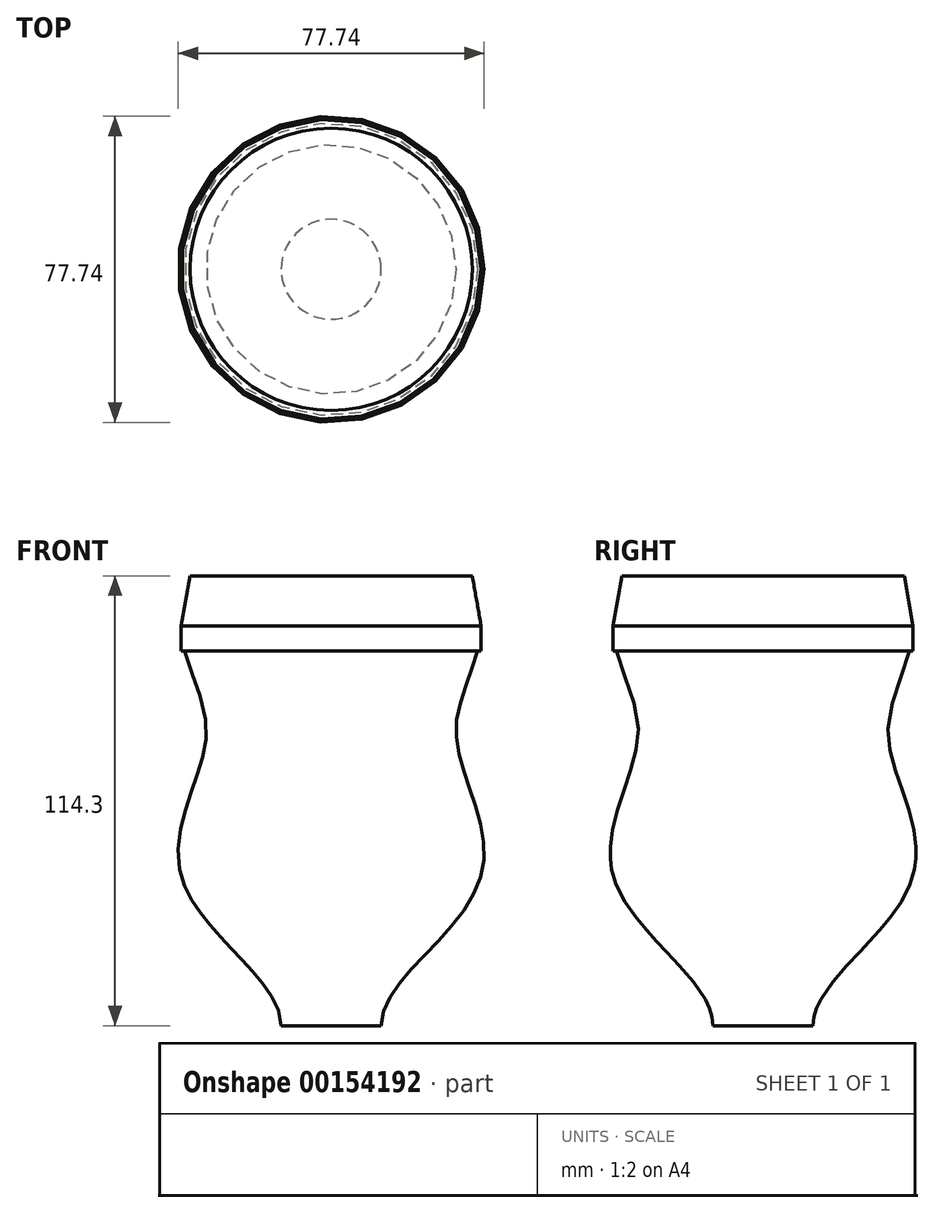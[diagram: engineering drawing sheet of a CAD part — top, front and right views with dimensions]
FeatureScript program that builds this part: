
annotation { "Feature Type Name" : "Feature", "Feature Type Description" : "" }
export const myFeature = defineFeature(function(context is Context, id is Id, definition is map)
    precondition{}
    {
        {
            var Q0;
            Q0=qCreatedBy(makeId("Top.planeOp"),FACE);
            var sketch = newSketch(context, id + "F0", { "sketchPlane" : qUnion([Q0])});
            skCircle(sketch, "E0", {"center": v(0, 0) * mm, "radius": 38.1 * mm});
            skSolve(sketch);
        }
        {
            var Q0;
            Q0=qCreatedBy(makeId("Top.planeOp"),FACE);
            cPlane(context, id + "F1", {"entities" : qUnion([Q0]), "cplaneType" : CPlaneType.OFFSET, "offset" : 25.4 * mm, "oppositeDirection" : true, "width" : 152.4 * mm, "height" : 152.4 * mm});
        }
        {
            var Q0;
            Q0=qCreatedBy(id+"F1.planeOp",FACE);
            var sketch = newSketch(context, id + "F2", { "sketchPlane" : qUnion([Q0])});
            skCircle(sketch, "E1", {"center": v(0, 0) * mm, "radius": 31.75 * mm});
            skSolve(sketch);
        }
        {
            var Q0;
            Q0=qCreatedBy(id+"F1.planeOp",FACE);
            cPlane(context, id + "F3", {"entities" : qUnion([Q0]), "cplaneType" : CPlaneType.OFFSET, "offset" : 25.4 * mm, "oppositeDirection" : true, "width" : 152.4 * mm, "height" : 152.4 * mm});
        }
        {
            var Q0;
            Q0=qCreatedBy(id+"F3.planeOp",FACE);
            var sketch = newSketch(context, id + "F4", { "sketchPlane" : qUnion([Q0])});
            skCircle(sketch, "E2", {"center": v(0, 0) * mm, "radius": 38.1 * mm});
            skSolve(sketch);
        }
        {
            var Q0;
            Q0=qCreatedBy(id+"F3.planeOp",FACE);
            cPlane(context, id + "F5", {"entities" : qUnion([Q0]), "cplaneType" : CPlaneType.OFFSET, "offset" : 12.7 * mm, "oppositeDirection" : true, "width" : 152.4 * mm, "height" : 152.4 * mm});
        }
        {
            var Q0;
            Q0=qCreatedBy(id+"F5.planeOp",FACE);
            var sketch = newSketch(context, id + "F6", { "sketchPlane" : qUnion([Q0])});
            skCircle(sketch, "E3", {"center": v(0, 0) * mm, "radius": 38.1 * mm});
            skSolve(sketch);
        }
        {
            var Q0;
            Q0=qCreatedBy(id+"F5.planeOp",FACE);
            cPlane(context, id + "F7", {"entities" : qUnion([Q0]), "cplaneType" : CPlaneType.OFFSET, "offset" : 38.1 * mm, "oppositeDirection" : true, "width" : 152.4 * mm, "height" : 152.4 * mm});
        }
        {
            var Q0;
            Q0=qCreatedBy(id+"F7.planeOp",FACE);
            var sketch = newSketch(context, id + "F8", { "sketchPlane" : qUnion([Q0])});
            skCircle(sketch, "E4", {"center": v(0, 0) * mm, "radius": 12.7 * mm});
            skSolve(sketch);
        }
        {
            var Q0;
            Q0=makeQuery(id+"F0.imprint","IMPRINT",FACE,{"disambiguationData":[TD([[makeQuery(id+"F0.imprint","IMPRINT",EDGE,{"derivedFrom":sQuery(id+"F0.wireOp",EDGE,"E0")}),1.0]])]});
            var Q1;
            Q1=makeQuery(id+"F2.imprint","IMPRINT",FACE,{"disambiguationData":[TD([[makeQuery(id+"F2.imprint","IMPRINT",EDGE,{"derivedFrom":sQuery(id+"F2.wireOp",EDGE,"E1")}),1.0]])]});
            var Q2;
            Q2=makeQuery(id+"F4.imprint","IMPRINT",FACE,{"disambiguationData":[TD([[makeQuery(id+"F4.imprint","IMPRINT",EDGE,{"derivedFrom":sQuery(id+"F4.wireOp",EDGE,"E2")}),1.0]])]});
            var Q3;
            Q3=makeQuery(id+"F6.imprint","IMPRINT",FACE,{"disambiguationData":[TD([[makeQuery(id+"F6.imprint","IMPRINT",EDGE,{"derivedFrom":sQuery(id+"F6.wireOp",EDGE,"E3")}),1.0]])]});
            var Q4;
            Q4=makeQuery(id+"F8.imprint","IMPRINT",FACE,{"disambiguationData":[TD([[makeQuery(id+"F8.imprint","IMPRINT",EDGE,{"derivedFrom":sQuery(id+"F8.wireOp",EDGE,"E4")}),1.0]])]});
            var Q5;
            Q5=sQuery(id+"F0.wireOp",EDGE,"E0");
            var Q6;
            Q6=sQuery(id+"F2.wireOp",EDGE,"E1");
            var Q7;
            Q7=sQuery(id+"F4.wireOp",EDGE,"E2");
            var Q8;
            Q8=sQuery(id+"F6.wireOp",EDGE,"E3");
            var Q9;
            Q9=sQuery(id+"F8.wireOp",EDGE,"E4");
            var Q10;
            Q10=sQuery(id+"F0.wireOp",VERTEX,"E0.center");
            var Q11;
            Q11=sQuery(id+"F2.wireOp",VERTEX,"E1.center");
            var Q12;
            Q12=sQuery(id+"F4.wireOp",VERTEX,"E2.center");
            var Q13;
            Q13=sQuery(id+"F6.wireOp",VERTEX,"E3.center");
            var Q14;
            Q14=sQuery(id+"F8.wireOp",VERTEX,"E4.center");
            loft(context, id + "F9", {"startCondition" : LoftEndDerivativeType.NORMAL_TO_PROFILE, "startMagnitude" : 1, "endCondition" : LoftEndDerivativeType.NORMAL_TO_PROFILE, "endMagnitude" : 1, "sheetProfilesArray" : [{ "sheetProfileEntities" : qUnion([Q0]) }, { "sheetProfileEntities" : qUnion([Q1]) }, { "sheetProfileEntities" : qUnion([Q2]) }, { "sheetProfileEntities" : qUnion([Q3]) }, { "sheetProfileEntities" : qUnion([Q4]) }], "wireProfilesArray" : [{ "wireProfileEntities" : qUnion([Q5]) }, { "wireProfileEntities" : qUnion([Q6]) }, { "wireProfileEntities" : qUnion([Q7]) }, { "wireProfileEntities" : qUnion([Q8]) }, { "wireProfileEntities" : qUnion([Q9]) }], "connections" : [{ "connectionEntities" : qUnion([Q10, Q11, Q12, Q13, Q14]), "connectionEdgeQueries" : qUnion([]), "connectionEdgeParameters" : [] }]});
        }
        {
            var Q0;
            Q0=qCreatedBy(makeId("Top.planeOp"),FACE);
            var sketch = newSketch(context, id + "F10", { "sketchPlane" : qUnion([Q0])});
            skCircle(sketch, "E5", {"center": v(0, 0) * mm, "radius": 38.1 * mm});
            skSolve(sketch);
        }
        {
            var Q0;
            Q0 = qSketchRegion(id + "F10", true);
            var Q1;
            Q1=sQuery(id+"F10.wireOp",EDGE,"E5");
            extrude(context, id + "F11", {"entities" : qUnion([Q0]), "operationType" : NewBodyOperationType.ADD, "surfaceEntities" : qUnion([Q1]), "depth" : 12.7 * mm, "hasDraft" : true, "draftAngle" : 10 * degree, "draftPullDirection" : true, "hasSecondDirection" : true, "secondDirectionOppositeDirection" : true, "secondDirectionDepth" : 6.35 * mm});
        }
    });
